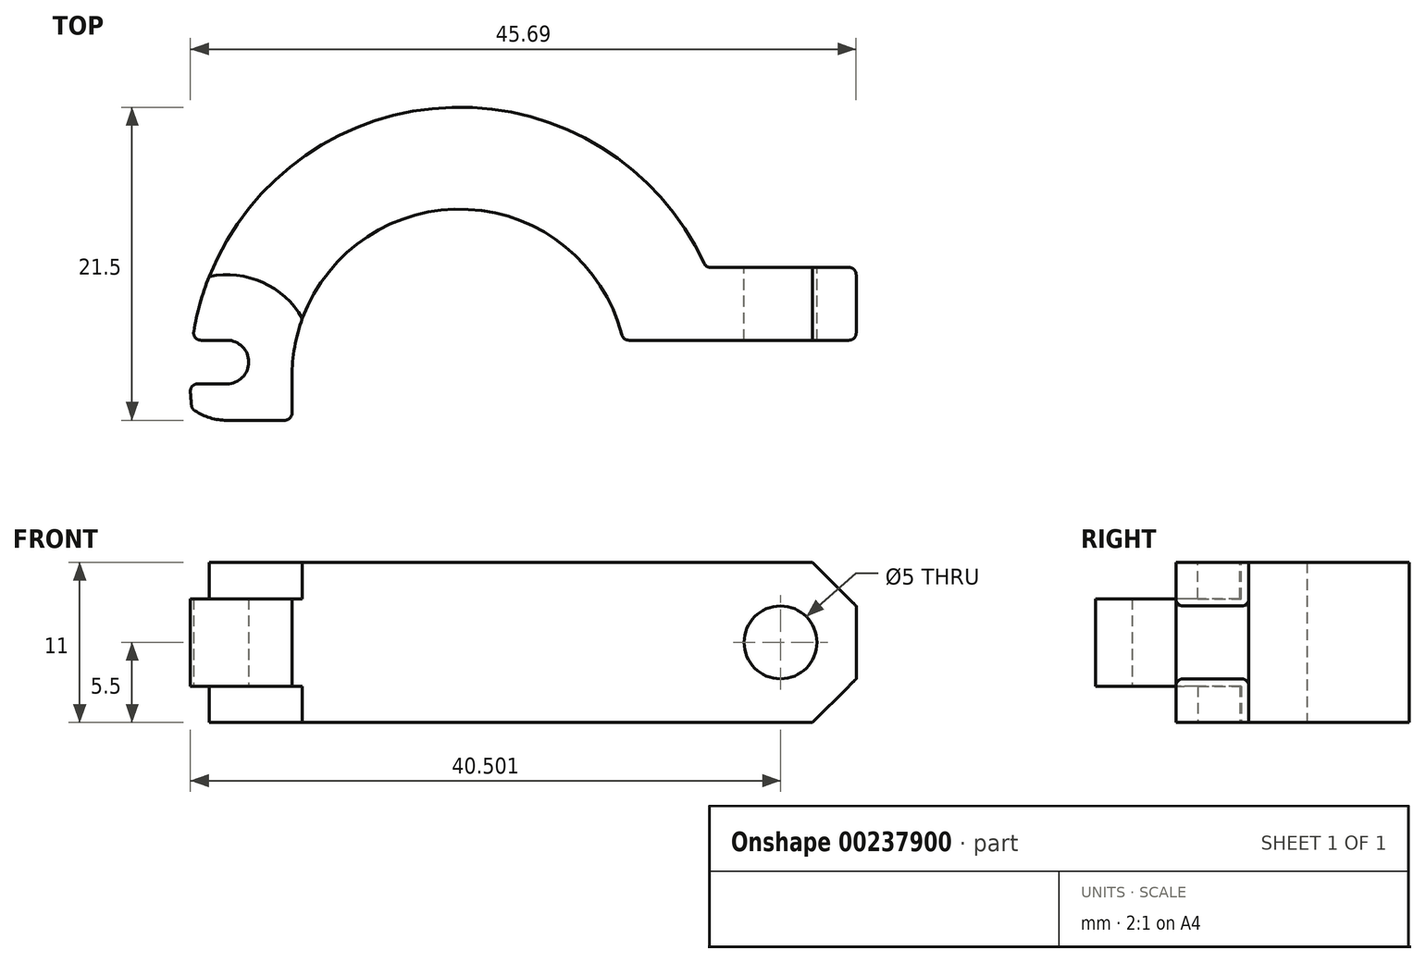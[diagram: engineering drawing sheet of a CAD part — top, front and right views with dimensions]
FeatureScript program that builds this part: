
annotation { "Feature Type Name" : "Feature", "Feature Type Description" : "" }
export const myFeature = defineFeature(function(context is Context, id is Id, definition is map)
    precondition{}
    {
        {
            var Q0;
            Q0=qCreatedBy(makeId("Top.planeOp"),FACE);
            var sketch = newSketch(context, id + "F0", { "sketchPlane" : qUnion([Q0])});
            skArc(sketch, "E0", {"start": v(11.22, 2.5) * mm, "mid": v(-1.26, 11.43) * mm, "end": v(-11.5, 0) * mm});
            skLineSegment(sketch, "E1", {"start": v(11.22, 2.5) * mm, "end": v(27.22, 2.5) * mm});
            skLineSegment(sketch, "E2", {"start": v(27.22, 2.5) * mm, "end": v(27.22, 7.5) * mm});
            skLineSegment(sketch, "E3", {"start": v(27.22, 7.5) * mm, "end": v(16.91, 7.5) * mm});
            skArc(sketch, "E4", {"start": v(16.91, 7.5) * mm, "mid": v(-2.6, 18.32) * mm, "end": v(-18.33, 2.5) * mm});
            skLineSegment(sketch, "E5", {"start": v(-15.97, 2.5) * mm, "end": v(-18.33, 2.5) * mm});
            skLineSegment(sketch, "E6", {"start": v(-15.97, -0.5) * mm, "end": v(-18.5, -0.5) * mm});
            skLineSegment(sketch, "E7", {"start": v(-15.97, -3) * mm, "end": v(-11.5, -3) * mm});
            skLineSegment(sketch, "E8", {"start": v(-11.5, -3) * mm, "end": v(-11.5, 0) * mm});
            skArc(sketch, "E9.trimOffspring", {"start": v(-18.5, -0.5) * mm, "mid": v(-18.45, -1.35) * mm, "end": v(-18.37, -2.2) * mm});
            skArc(sketch, "E10", {"start": v(-15.97, -0.5) * mm, "mid": v(-14.47, 1) * mm, "end": v(-15.97, 2.5) * mm});
            skArc(sketch, "E11", {"start": v(-18.37, -2.2) * mm, "mid": v(-17.23, -2.8) * mm, "end": v(-15.97, -3) * mm});
            skSolve(sketch);
        }
        {
            var Q0;
            Q0=makeQuery(id+"F0.imprint","IMPRINT",FACE,{"disambiguationData":[TD([[makeQuery(id+"F0.imprint","IMPRINT",EDGE,{"derivedFrom":sQuery(id+"F0.wireOp",EDGE,"E0")}),-1.0]])]});
            extrude(context, id + "F1", {"entities" : qUnion([Q0]), "depth" : 5.5 * mm, "offsetDistance" : 25 * mm});
        }
        {
            var Q0;
            Q0=makeQuery(id+"F1.opExtrude","CAP_FACE",FACE,{"disambiguationData":[OSD([sQuery(id+"F0.wireOp",EDGE,"E0"),sQuery(id+"F0.wireOp",EDGE,"E1"),sQuery(id+"F0.wireOp",EDGE,"E2"),sQuery(id+"F0.wireOp",EDGE,"E3"),sQuery(id+"F0.wireOp",EDGE,"E4"),sQuery(id+"F0.wireOp",EDGE,"E5"),sQuery(id+"F0.wireOp",EDGE,"E6"),sQuery(id+"F0.wireOp",EDGE,"E7"),sQuery(id+"F0.wireOp",EDGE,"E8"),sQuery(id+"F0.wireOp",EDGE,"E9.trimOffspring"),sQuery(id+"F0.wireOp",EDGE,"yo5YGE1G-0tL6-bubH-kUhE-XeJeWRATf6gU")])],"isStart":false});
            var sketch = newSketch(context, id + "F2", { "sketchPlane" : qUnion([Q0])});
            skLineSegment(sketch, "E12.0", {"start": v(-18.5, -0.5) * mm, "end": v(-18.5, -0.5) * mm});
            skCircle(sketch, "E13", {"center": v(-15.97, 1) * mm, "radius": 6 * mm});
            skSolve(sketch);
        }
        {
            var Q0;
            Q0=makeQuery(id+"F2.imprint","IMPRINT",FACE,{"disambiguationData":[TD([[makeQuery(id+"F2.imprint","IMPRINT",EDGE,{"derivedFrom":sQuery(id+"F2.wireOp",EDGE,"w3Alo0tF-pYE4-U33b-0OhH-kVYdrlR0At18")}),-1.0]])]});
            var Q1;
            {var subQ0=makeQuery(id+"F1.opExtrude","CAP_EDGE",EDGE,{"disambiguationData":[OSD([sQuery(id+"F0.wireOp",EDGE,"E5")])],"isStart":false});Q1=makeQuery(id+"F2.imprint","IMPRINT",FACE,{"disambiguationData":[TD([[makeQuery(id+"F2.imprint","IMPRINT",EDGE,{"derivedFrom":subQ0}),-1.0]])]});}
            extrude(context, id + "F3", {"entities" : qUnion([Q0, Q1]), "operationType" : NewBodyOperationType.REMOVE, "oppositeDirection" : true, "depth" : 2.5 * mm, "offsetDistance" : 25 * mm});
        }
        {
            var Q0;
            Q0=makeQuery(id+"F1.opExtrude","SWEPT_BODY",BODY,{"disambiguationData":[OSD([sQuery(id+"F0.wireOp",EDGE,"E0"),sQuery(id+"F0.wireOp",EDGE,"E1"),sQuery(id+"F0.wireOp",EDGE,"E2"),sQuery(id+"F0.wireOp",EDGE,"E3"),sQuery(id+"F0.wireOp",EDGE,"E4"),sQuery(id+"F0.wireOp",EDGE,"E5"),sQuery(id+"F0.wireOp",EDGE,"E6"),sQuery(id+"F0.wireOp",EDGE,"E7"),sQuery(id+"F0.wireOp",EDGE,"E8"),sQuery(id+"F0.wireOp",EDGE,"E9.trimOffspring"),sQuery(id+"F0.wireOp",EDGE,"yo5YGE1G-0tL6-bubH-kUhE-XeJeWRATf6gU")])]});
            var Q1;
            Q1=qCreatedBy(makeId("Top.planeOp"),FACE);
            mirror(context, id + "F4", {"operationType" : NewBodyOperationType.ADD, "entities" : qUnion([Q0]), "mirrorPlane" : qUnion([Q1])});
        }
        {
            var Q0;
            {var subQ0=makeQuery(id+"F1.opExtrude","SWEPT_FACE",FACE,{"disambiguationData":[OSD([sQuery(id+"F0.wireOp",EDGE,"E3")])]});Q0=makeQuery(id+"F4.boolean.opBoolean","MERGE",FACE,{"derivedFrom":[subQ0,makeQuery(id+"F4.opPattern","COPY",FACE,{"derivedFrom":subQ0,"instanceName":"1"})]});}
            var sketch = newSketch(context, id + "F5", { "sketchPlane" : qUnion([Q0])});
            skCircle(sketch, "E14", {"center": v(-22.03, 0) * mm, "radius": 2.5 * mm});
            skSolve(sketch);
        }
        {
            var Q0;
            Q0=makeQuery(id+"F5.imprint","IMPRINT",FACE,{"disambiguationData":[TD([[makeQuery(id+"F5.imprint","IMPRINT",EDGE,{"derivedFrom":sQuery(id+"F5.wireOp",EDGE,"E14")}),1.0]])]});
            extrude(context, id + "F6", {"entities" : qUnion([Q0]), "operationType" : NewBodyOperationType.REMOVE, "endBound" : BoundingType.UP_TO_NEXT, "oppositeDirection" : true, "depth" : 25 * mm, "offsetDistance" : 25 * mm});
        }
        {
            var Q0;
            Q0=makeQuery(id+"F1.opExtrude","CAP_EDGE",EDGE,{"disambiguationData":[OSD([sQuery(id+"F0.wireOp",EDGE,"E2")])],"isStart":false});
            var Q1;
            Q1=makeQuery(id+"F4.opPattern","COPY",EDGE,{"derivedFrom":makeQuery(id+"F1.opExtrude","CAP_EDGE",EDGE,{"disambiguationData":[OSD([sQuery(id+"F0.wireOp",EDGE,"E2")])],"isStart":false}),"instanceName":"1"});
            chamfer(context, id + "F7", {"entities" : qUnion([Q0, Q1]), "width" : 3 * mm, "tangentPropagation" : true});
        }
        {
            var Q0;
            {var subQ0=makeQuery(id+"F1.opExtrude","SWEPT_EDGE",EDGE,{"disambiguationData":[OSD([sQuery(id+"F0.wireOp",EDGE,"E7"),sQuery(id+"F0.wireOp",EDGE,"E8")])]});Q0=makeQuery(id+"F4.boolean.opBoolean","MERGE",EDGE,{"derivedFrom":[subQ0,makeQuery(id+"F4.opPattern","COPY",EDGE,{"derivedFrom":subQ0,"instanceName":"1"})]});}
            var Q1;
            Q1=makeQuery(id+"F3.boolean.opBoolean","COPY",EDGE,{"derivedFrom":makeQuery(id+"F3.opExtrude","SWEPT_EDGE",EDGE,{"disambiguationData":[OSD([sQuery(id+"F0.wireOp",EDGE,"E0"),sQuery(id+"F2.wireOp",EDGE,"E13")])]})});
            var Q2;
            Q2=makeQuery(id+"F4.opPattern","COPY",EDGE,{"derivedFrom":makeQuery(id+"F3.boolean.opBoolean","COPY",EDGE,{"derivedFrom":makeQuery(id+"F3.opExtrude","SWEPT_EDGE",EDGE,{"disambiguationData":[OSD([sQuery(id+"F0.wireOp",EDGE,"E0"),sQuery(id+"F2.wireOp",EDGE,"E13")])]})}),"instanceName":"1"});
            var Q3;
            Q3=makeQuery(id+"F3.boolean.opBoolean","COPY",EDGE,{"derivedFrom":makeQuery(id+"F3.opExtrude","SWEPT_EDGE",EDGE,{"disambiguationData":[OSD([sQuery(id+"F0.wireOp",EDGE,"E4"),sQuery(id+"F2.wireOp",EDGE,"E13")])]})});
            var Q4;
            Q4=makeQuery(id+"F4.opPattern","COPY",EDGE,{"derivedFrom":makeQuery(id+"F3.boolean.opBoolean","COPY",EDGE,{"derivedFrom":makeQuery(id+"F3.opExtrude","SWEPT_EDGE",EDGE,{"disambiguationData":[OSD([sQuery(id+"F0.wireOp",EDGE,"E4"),sQuery(id+"F2.wireOp",EDGE,"E13")])]})}),"instanceName":"1"});
            var Q5;
            {var subQ0=makeQuery(id+"F1.opExtrude","SWEPT_EDGE",EDGE,{"disambiguationData":[OSD([sQuery(id+"F0.wireOp",EDGE,"E9.trimOffspring"),sQuery(id+"F0.wireOp",EDGE,"E11")])]});Q5=makeQuery(id+"F4.boolean.opBoolean","MERGE",EDGE,{"derivedFrom":[subQ0,makeQuery(id+"F4.opPattern","COPY",EDGE,{"derivedFrom":subQ0,"instanceName":"1"})]});}
            var Q6;
            {var subQ0=makeQuery(id+"F1.opExtrude","SWEPT_EDGE",EDGE,{"disambiguationData":[OSD([sQuery(id+"F0.wireOp",EDGE,"E6"),sQuery(id+"F0.wireOp",EDGE,"E9.trimOffspring")])]});Q6=makeQuery(id+"F4.boolean.opBoolean","MERGE",EDGE,{"derivedFrom":[subQ0,makeQuery(id+"F4.opPattern","COPY",EDGE,{"derivedFrom":subQ0,"instanceName":"1"})]});}
            var Q7;
            {var subQ0=makeQuery(id+"F1.opExtrude","SWEPT_EDGE",EDGE,{"disambiguationData":[OSD([sQuery(id+"F0.wireOp",EDGE,"E4"),sQuery(id+"F0.wireOp",EDGE,"E5")])]});Q7=makeQuery(id+"F4.boolean.opBoolean","MERGE",EDGE,{"derivedFrom":[subQ0,makeQuery(id+"F4.opPattern","COPY",EDGE,{"derivedFrom":subQ0,"instanceName":"1"})]});}
            var Q8;
            {var subQ0=makeQuery(id+"F1.opExtrude","SWEPT_EDGE",EDGE,{"disambiguationData":[OSD([sQuery(id+"F0.wireOp",EDGE,"E0"),sQuery(id+"F0.wireOp",EDGE,"E1")])]});Q8=makeQuery(id+"F4.boolean.opBoolean","MERGE",EDGE,{"derivedFrom":[subQ0,makeQuery(id+"F4.opPattern","COPY",EDGE,{"derivedFrom":subQ0,"instanceName":"1"})]});}
            var Q9;
            {var subQ0=makeQuery(id+"F1.opExtrude","SWEPT_EDGE",EDGE,{"disambiguationData":[OSD([sQuery(id+"F0.wireOp",EDGE,"E3"),sQuery(id+"F0.wireOp",EDGE,"E4")])]});Q9=makeQuery(id+"F4.boolean.opBoolean","MERGE",EDGE,{"derivedFrom":[subQ0,makeQuery(id+"F4.opPattern","COPY",EDGE,{"derivedFrom":subQ0,"instanceName":"1"})]});}
            var Q10;
            {var subQ0=makeQuery(id+"F1.opExtrude","SWEPT_EDGE",EDGE,{"disambiguationData":[OSD([sQuery(id+"F0.wireOp",EDGE,"E1"),sQuery(id+"F0.wireOp",EDGE,"E2")])]});Q10=makeQuery(id+"F4.boolean.opBoolean","MERGE",EDGE,{"derivedFrom":[subQ0,makeQuery(id+"F4.opPattern","COPY",EDGE,{"derivedFrom":subQ0,"instanceName":"1"})]});}
            var Q11;
            {var subQ0=makeQuery(id+"F1.opExtrude","SWEPT_EDGE",EDGE,{"disambiguationData":[OSD([sQuery(id+"F0.wireOp",EDGE,"E2"),sQuery(id+"F0.wireOp",EDGE,"E3")])]});Q11=makeQuery(id+"F4.boolean.opBoolean","MERGE",EDGE,{"derivedFrom":[subQ0,makeQuery(id+"F4.opPattern","COPY",EDGE,{"derivedFrom":subQ0,"instanceName":"1"})]});}
            fillet(context, id + "F8", {"entities" : qUnion([Q0, Q1, Q2, Q3, Q4, Q5, Q6, Q7, Q8, Q9, Q10, Q11]), "radius" : 0.5 * mm, "tangentPropagation" : true, "allowEdgeOverflow" : false});
        }
    });
